# Revit family: LED WALL WASHER SLIM_LKPA3PB0620.30
name_source: partatom
category: Luminarias
units: mm (PartAtom-declared; Revit-internal decimal feet)

## family parameters
Compartido = No
Corte con vacíos al cargar = No
Cota de conector redondo = Diámetro de uso
Origen de luz = Sí
Punto de cálculo de habitación = No
Se basa en plano de trabajo = Sí
Siempre vertical = No
Tipo de pieza = Normal

## types (1)
- REFL_LKPA3PB0620.30
    Cambio de temperatura de color de luz atenuada = Curva de lámpara incandescente
    Comentarios de vataje = 24V
    Descripción = LUMINARIA TIPO REFLECTOR SPOT, WALL WASHER , CUERPO EN ALUMINIO EXTRUIDO CUBIERTO CON POLVO GRIS OSCURO Y VIDRIO TEMPLADO DE 4MM, CUENTA CON 6 LED TIPO PROLIGHT RGBW R=299mA G=352mA B=350Ma W=349mA CON UN CONSUMO TOTAL DE 32W, 1000 LUMENES, , IRC 80, IP 66, IK08,  CABLE H05RN DE 2M, APERTURA DE 30 GRADOS EN STOCK, ALIMENTADA A 24V. REQUIERE ACCESORIOS.
    Elevación por defecto = 0 mm  [stored 0 ft]
    Fabricante = BRILLANT
    Filtro de color = 16777215
    Longitud de símbolo de origen de luz = 500 mm  [stored 1.64042 ft]
    Lámpara = PROLIGHT RGBW
    Modelo = LKPA3PB0620.30
    Watt per fixture = 32
    Ángulo de campo de foco = 30.00°
    Ángulo de enfoque = 30.00°
    Ángulo de inclinación = 30.00°

note: [stored X ft] marks values corroborated as IEEE doubles in the binary element streams (Revit-internal decimal feet)

## geometry (parser evidence)
native form markers: Blend x2
no freeform markers — native parametric forms only
